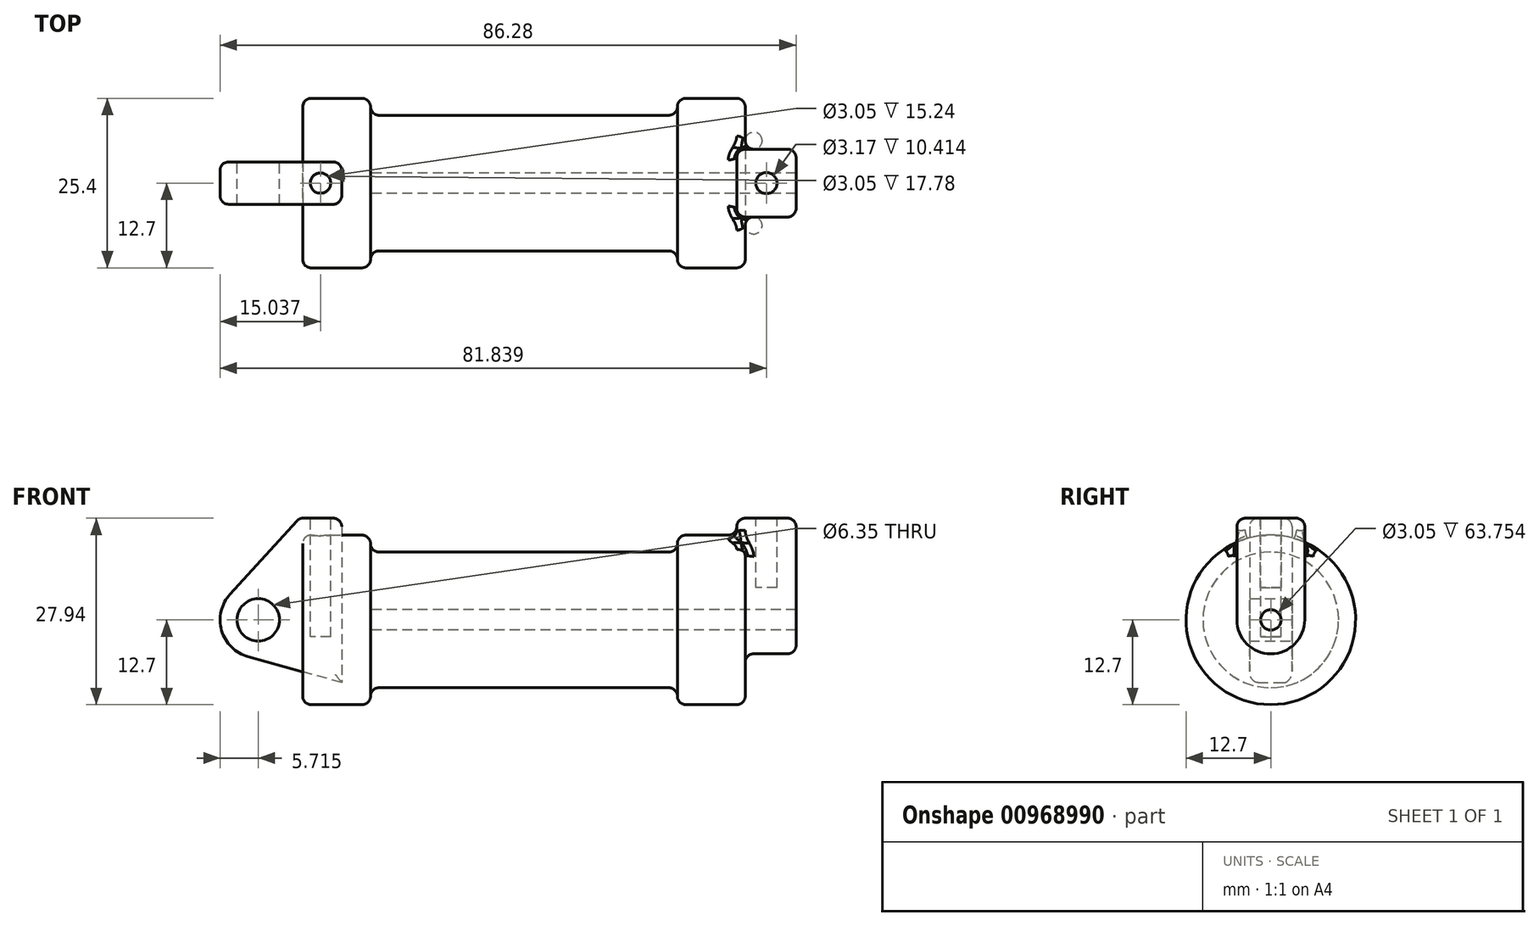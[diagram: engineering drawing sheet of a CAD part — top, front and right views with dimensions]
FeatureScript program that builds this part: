
annotation { "Feature Type Name" : "Feature", "Feature Type Description" : "" }
export const myFeature = defineFeature(function(context is Context, id is Id, definition is map)
    precondition{}
    {
        {
            var Q0;
            Q0=qCreatedBy(makeId("Front.planeOp"),FACE);
            var sketch = newSketch(context, id + "F0", { "sketchPlane" : qUnion([Q0])});
            skLineSegment(sketch, "E0", {"start": v(0, 0) * mm, "end": v(0, 12.7) * mm});
            skLineSegment(sketch, "E1", {"start": v(0, 12.7) * mm, "end": v(10.16, 12.7) * mm});
            skLineSegment(sketch, "E2", {"start": v(10.16, 12.7) * mm, "end": v(10.16, 10.16) * mm});
            skLineSegment(sketch, "E3", {"start": v(10.16, 10.16) * mm, "end": v(56.13, 10.16) * mm});
            skLineSegment(sketch, "E4", {"start": v(56.13, 10.16) * mm, "end": v(56.13, 12.7) * mm});
            skLineSegment(sketch, "E5", {"start": v(56.13, 12.7) * mm, "end": v(66.3, 12.7) * mm});
            skLineSegment(sketch, "E6", {"start": v(66.3, 12.7) * mm, "end": v(66.3, 0) * mm});
            skLineSegment(sketch, "E7", {"start": v(66.3, 0) * mm, "end": v(0, 0) * mm});
            skLineSegment(sketch, "E8", {"start": v(5.84, 15.24) * mm, "end": v(-0.5, 15.24) * mm});
            skLineSegment(sketch, "E9", {"start": v(-0.5, 15.24) * mm, "end": v(-10.88, 3.85) * mm});
            skLineSegment(sketch, "E10", {"start": v(0, 0) * mm, "end": v(-6.65, 0) * mm});
            skCircle(sketch, "E11", {"center": v(-6.65, 0) * mm, "radius": 5.72 * mm});
            skCircle(sketch, "E12", {"center": v(-6.65, 0) * mm, "radius": 3.18 * mm});
            skLineSegment(sketch, "E13", {"start": v(5.84, 15.24) * mm, "end": v(5.84, -9.4) * mm});
            skLineSegment(sketch, "E14", {"start": v(5.84, -9.4) * mm, "end": v(-8.18, -5.5) * mm});
            skSolve(sketch);
        }
        {
            var Q0;
            {var subQ0=sQuery(id+"F0.wireOp",EDGE,"E0");Q0=makeQuery(id+"F0.imprint","IMPRINT",FACE,{"disambiguationData":[TD([[makeQuery(id+"F0.imprint","IMPRINT",EDGE,{"derivedFrom":subQ0}),-1.0]])]});}
            var Q1;
            {var subQ1=sQuery(id+"F0.wireOp",EDGE,"E0");Q1=makeQuery(id+"F0.imprint","IMPRINT",FACE,{"disambiguationData":[TD([[makeQuery(id+"F0.imprint","IMPRINT",EDGE,{"derivedFrom":subQ1}),1.0]])]});}
            var Q2;
            {var subQ5=sQuery(id+"F0.wireOp",EDGE,"E12");Q2=makeQuery(id+"F0.imprint","IMPRINT",FACE,{"disambiguationData":[TD([[makeQuery(id+"F0.imprint","IMPRINT",EDGE,{"derivedFrom":subQ5}),-1.0]])]});}
            var Q3;
            {var subQ0=sQuery(id+"F0.wireOp",EDGE,"E14");Q3=makeQuery(id+"F0.imprint","IMPRINT",FACE,{"disambiguationData":[TD([[makeQuery(id+"F0.imprint","IMPRINT",EDGE,{"derivedFrom":subQ0}),-1.0]])]});}
            extrude(context, id + "F1", {"entities" : qUnion([Q0, Q1, Q2, Q3]), "endBound" : BoundingType.SYMMETRIC, "depth" : 6.35 * mm, "offsetDistance" : 25.4 * mm});
        }
        {
            var Q0;
            {var subQ0=sQuery(id+"F0.wireOp",EDGE,"E0");Q0=makeQuery(id+"F0.imprint","IMPRINT",FACE,{"disambiguationData":[TD([[makeQuery(id+"F0.imprint","IMPRINT",EDGE,{"derivedFrom":subQ0}),-1.0]])]});}
            var Q1;
            {var subQ0=sQuery(id+"F0.wireOp",EDGE,"E2");Q1=makeQuery(id+"F0.imprint","IMPRINT",FACE,{"disambiguationData":[TD([[makeQuery(id+"F0.imprint","IMPRINT",EDGE,{"derivedFrom":subQ0}),-1.0]])]});}
            var Q2;
            Q2=sQuery(id+"F0.wireOp",EDGE,"E7");
            revolve(context, id + "F2", {"surfaceOperationType" : NewSurfaceOperationType.NEW, "entities" : qUnion([Q0, Q1]), "axis" : qUnion([Q2]), "revolveType" : RevolveType.FULL});
        }
        {
            var Q0;
            Q0=makeQuery(id+"F2.opRevolve","SWEPT_FACE",FACE,{"disambiguationData":[OSD([sQuery(id+"F0.wireOp",EDGE,"E6")])]});
            var sketch = newSketch(context, id + "F3", { "sketchPlane" : qUnion([Q0])});
            skCircle(sketch, "E15", {"center": v(0, 0) * mm, "radius": 1.52 * mm});
            skCircle(sketch, "E16", {"center": v(0, 0) * mm, "radius": 5.08 * mm});
            skLineSegment(sketch, "E17", {"start": v(-5.08, 0) * mm, "end": v(-5.08, 15.24) * mm});
            skLineSegment(sketch, "E18", {"start": v(-5.08, 15.24) * mm, "end": v(5.08, 15.24) * mm});
            skLineSegment(sketch, "E19", {"start": v(5.08, 15.24) * mm, "end": v(5.08, 0) * mm});
            skSolve(sketch);
        }
        {
            var Q0;
            Q0 = qSketchRegion(id + "F3", true);
            extrude(context, id + "F4", {"entities" : qUnion([Q0]), "operationType" : NewBodyOperationType.ADD, "depth" : 7.62 * mm, "offsetDistance" : 25.4 * mm, "hasSecondDirection" : true, "secondDirectionOppositeDirection" : true, "secondDirectionDepth" : 1.27 * mm});
        }
        {
            var Q0;
            Q0=makeQuery(id+"F4.boolean.opBoolean","SPLIT",FACE,{"disambiguationData":[TD([makeQuery(id+"F4.opExtrude","SWEPT_FACE",FACE,{"disambiguationData":[OSD([sQuery(id+"F3.wireOp",EDGE,"E15")])]})])],"derivedFrom":makeQuery(id+"F2.opRevolve","SWEPT_FACE",FACE,{"disambiguationData":[OSD([sQuery(id+"F0.wireOp",EDGE,"E6")])]})});
            var Q1;
            Q1=makeQuery(id+"F2.opRevolve","SWEPT_FACE",FACE,{"disambiguationData":[OSD([sQuery(id+"F0.wireOp",EDGE,"E2")])]});
            extrude(context, id + "F5", {"entities" : qUnion([Q0]), "operationType" : NewBodyOperationType.REMOVE, "endBound" : BoundingType.UP_TO_SURFACE, "oppositeDirection" : true, "depth" : 25.4 * mm, "endBoundEntityFace" : qUnion([Q1]), "offsetDistance" : 25.4 * mm});
        }
        {
            var Q0;
            Q0=makeQuery(id+"F1.opExtrude","SWEPT_FACE",FACE,{"disambiguationData":[OSD([sQuery(id+"F0.wireOp",EDGE,"E8")])]});
            var sketch = newSketch(context, id + "F6", { "sketchPlane" : qUnion([Q0])});
            skCircle(sketch, "E20", {"center": v(2.67, 0) * mm, "radius": 1.52 * mm});
            skLineSegment(sketch, "E21", {"start": v(2.67, 0) * mm, "end": v(5.84, 0) * mm, "construction": true});
            skLineSegment(sketch, "E22", {"start": v(5.84, 0) * mm, "end": v(-0.5, 0) * mm, "construction": true});
            skLineSegment(sketch, "E23", {"start": v(-0.5, 0) * mm, "end": v(2.67, 0) * mm, "construction": true});
            skSolve(sketch);
        }
        {
            var Q0;
            Q0=makeQuery(id+"F6.imprint","IMPRINT",FACE,{"disambiguationData":[TD([[makeQuery(id+"F6.imprint","IMPRINT",EDGE,{"derivedFrom":sQuery(id+"F6.wireOp",EDGE,"E20")}),1.0]])]});
            extrude(context, id + "F7", {"entities" : qUnion([Q0]), "operationType" : NewBodyOperationType.REMOVE, "oppositeDirection" : true, "depth" : 17.78 * mm, "offsetDistance" : 25.4 * mm});
        }
        {
            var Q0;
            Q0=makeQuery(id+"F4.opExtrude","SWEPT_FACE",FACE,{"disambiguationData":[OSD([sQuery(id+"F3.wireOp",EDGE,"E18")])]});
            var sketch = newSketch(context, id + "F8", { "sketchPlane" : qUnion([Q0])});
            skCircle(sketch, "E24", {"center": v(69.47, 0) * mm, "radius": 1.59 * mm});
            skLineSegment(sketch, "E25", {"start": v(69.47, 0) * mm, "end": v(69.47, 5.08) * mm, "construction": true});
            skLineSegment(sketch, "E26", {"start": v(69.47, 0) * mm, "end": v(69.47, -5.08) * mm, "construction": true});
            skLineSegment(sketch, "E27", {"start": v(69.47, 0) * mm, "end": v(65.02, 0) * mm, "construction": true});
            skLineSegment(sketch, "E28", {"start": v(69.47, 0) * mm, "end": v(73.91, 0) * mm, "construction": true});
            skSolve(sketch);
        }
        {
            var Q0;
            Q0=makeQuery(id+"F8.imprint","IMPRINT",FACE,{"disambiguationData":[TD([[makeQuery(id+"F8.imprint","IMPRINT",EDGE,{"derivedFrom":sQuery(id+"F8.wireOp",EDGE,"E24")}),1.0]])]});
            extrude(context, id + "F9", {"entities" : qUnion([Q0]), "operationType" : NewBodyOperationType.REMOVE, "oppositeDirection" : true, "depth" : 10.4 * mm, "offsetDistance" : 25.4 * mm});
        }
        {
            var Q0;
            Q0=makeQuery(id+"F2.opRevolve","SWEPT_EDGE",EDGE,{"disambiguationData":[OSD([sQuery(id+"F0.wireOp",EDGE,"E0"),sQuery(id+"F0.wireOp",EDGE,"E1")])]});
            var Q1;
            Q1=makeQuery(id+"F2.opRevolve","SWEPT_EDGE",EDGE,{"disambiguationData":[OSD([sQuery(id+"F0.wireOp",EDGE,"E1"),sQuery(id+"F0.wireOp",EDGE,"E2")])]});
            var Q2;
            Q2=makeQuery(id+"F1.opExtrude","CAP_EDGE",EDGE,{"disambiguationData":[OSD([sQuery(id+"F0.wireOp",EDGE,"E8")])],"isStart":false});
            var Q3;
            Q3=makeQuery(id+"F1.opExtrude","CAP_EDGE",EDGE,{"disambiguationData":[OSD([sQuery(id+"F0.wireOp",EDGE,"E13")])],"isStart":false});
            var Q4;
            Q4=makeQuery(id+"F1.opExtrude","CAP_EDGE",EDGE,{"disambiguationData":[OSD([sQuery(id+"F0.wireOp",EDGE,"E9")])],"isStart":false});
            var Q5;
            Q5=makeQuery(id+"F1.opExtrude","SWEPT_EDGE",EDGE,{"disambiguationData":[OSD([sQuery(id+"F0.wireOp",EDGE,"E8"),sQuery(id+"F0.wireOp",EDGE,"E9")])]});
            var Q6;
            Q6=makeQuery(id+"F1.opExtrude","CAP_EDGE",EDGE,{"disambiguationData":[OSD([sQuery(id+"F0.wireOp",EDGE,"E8")])],"isStart":true});
            var Q7;
            Q7=makeQuery(id+"F1.opExtrude","CAP_EDGE",EDGE,{"disambiguationData":[OSD([sQuery(id+"F0.wireOp",EDGE,"E13")])],"isStart":true});
            var Q8;
            Q8=makeQuery(id+"F1.opExtrude","SWEPT_EDGE",EDGE,{"disambiguationData":[OSD([sQuery(id+"F0.wireOp",EDGE,"E8"),sQuery(id+"F0.wireOp",EDGE,"E13")])]});
            var Q9;
            Q9=makeQuery(id+"F1.opExtrude","CAP_EDGE",EDGE,{"disambiguationData":[OSD([sQuery(id+"F0.wireOp",EDGE,"E11")])],"isStart":false});
            var Q10;
            Q10=makeQuery(id+"F1.opExtrude","CAP_EDGE",EDGE,{"disambiguationData":[OSD([sQuery(id+"F0.wireOp",EDGE,"E11")])],"isStart":true});
            var Q11;
            Q11=makeQuery(id+"F1.opExtrude","CAP_EDGE",EDGE,{"disambiguationData":[OSD([sQuery(id+"F0.wireOp",EDGE,"E14")])],"isStart":false});
            var Q12;
            Q12=makeQuery(id+"F2.opRevolve","SWEPT_EDGE",EDGE,{"disambiguationData":[OSD([sQuery(id+"F0.wireOp",EDGE,"E2"),sQuery(id+"F0.wireOp",EDGE,"E3")])]});
            var Q13;
            Q13=makeQuery(id+"F2.opRevolve","SWEPT_EDGE",EDGE,{"disambiguationData":[OSD([sQuery(id+"F0.wireOp",EDGE,"E3"),sQuery(id+"F0.wireOp",EDGE,"E4")])]});
            var Q14;
            Q14=makeQuery(id+"F2.opRevolve","SWEPT_EDGE",EDGE,{"disambiguationData":[OSD([sQuery(id+"F0.wireOp",EDGE,"E4"),sQuery(id+"F0.wireOp",EDGE,"E5")])]});
            var Q15;
            Q15=makeQuery(id+"F2.opRevolve","SWEPT_EDGE",EDGE,{"disambiguationData":[OSD([sQuery(id+"F0.wireOp",EDGE,"E5"),sQuery(id+"F0.wireOp",EDGE,"E6")])]});
            var Q16;
            Q16=makeQuery(id+"F4.opExtrude","CAP_EDGE",EDGE,{"disambiguationData":[OSD([sQuery(id+"F3.wireOp",EDGE,"E17")])],"isStart":true});
            var Q17;
            Q17=makeQuery(id+"F4.opExtrude","SWEPT_EDGE",EDGE,{"disambiguationData":[OSD([sQuery(id+"F3.wireOp",EDGE,"E17"),sQuery(id+"F3.wireOp",EDGE,"E18")])]});
            var Q18;
            Q18=makeQuery(id+"F4.opExtrude","CAP_EDGE",EDGE,{"disambiguationData":[OSD([sQuery(id+"F3.wireOp",EDGE,"E17")])],"isStart":false});
            var Q19;
            Q19=makeQuery(id+"F4.boolean.opBoolean","SPLIT",FACE,{"disambiguationData":[TD([makeQuery(id+"F2.opRevolve","SWEPT_FACE",FACE,{"disambiguationData":[OSD([sQuery(id+"F0.wireOp",EDGE,"E5")])]})])],"derivedFrom":makeQuery(id+"F2.opRevolve","SWEPT_FACE",FACE,{"disambiguationData":[OSD([sQuery(id+"F0.wireOp",EDGE,"E6")])]})});
            var Q20;
            Q20=makeQuery(id+"F4.opExtrude","CAP_EDGE",EDGE,{"disambiguationData":[OSD([sQuery(id+"F3.wireOp",EDGE,"E16")])],"isStart":false});
            var Q21;
            Q21=makeQuery(id+"F4.opExtrude","CAP_EDGE",EDGE,{"disambiguationData":[OSD([sQuery(id+"F3.wireOp",EDGE,"E19")])],"isStart":false});
            var Q22;
            Q22=makeQuery(id+"F4.opExtrude","SWEPT_EDGE",EDGE,{"disambiguationData":[OSD([sQuery(id+"F3.wireOp",EDGE,"E18"),sQuery(id+"F3.wireOp",EDGE,"E19")])]});
            var Q23;
            Q23=makeQuery(id+"F4.opExtrude","CAP_EDGE",EDGE,{"disambiguationData":[OSD([sQuery(id+"F3.wireOp",EDGE,"E18")])],"isStart":false});
            var Q24;
            Q24=makeQuery(id+"F4.opExtrude","CAP_EDGE",EDGE,{"disambiguationData":[OSD([sQuery(id+"F3.wireOp",EDGE,"E18")])],"isStart":true});
            var Q25;
            Q25=makeQuery(id+"F4.opExtrude","CAP_EDGE",EDGE,{"disambiguationData":[OSD([sQuery(id+"F3.wireOp",EDGE,"E19")])],"isStart":true});
            var Q26;
            Q26=makeQuery(id+"F4.boolean.opBoolean","INTERSECT",EDGE,{"derivedFrom":[makeQuery(id+"F2.opRevolve","SWEPT_FACE",FACE,{"disambiguationData":[OSD([sQuery(id+"F0.wireOp",EDGE,"E5")])]}),makeQuery(id+"F4.opExtrude","CAP_FACE",FACE,{"disambiguationData":[OSD([sQuery(id+"F3.wireOp",EDGE,"E15"),sQuery(id+"F3.wireOp",EDGE,"E16"),sQuery(id+"F3.wireOp",EDGE,"E17"),sQuery(id+"F3.wireOp",EDGE,"E18"),sQuery(id+"F3.wireOp",EDGE,"E19")])],"isStart":true})]});
            var Q27;
            Q27=makeQuery(id+"F4.boolean.opBoolean","INTERSECT",EDGE,{"derivedFrom":[makeQuery(id+"F2.opRevolve","SWEPT_FACE",FACE,{"disambiguationData":[OSD([sQuery(id+"F0.wireOp",EDGE,"E5")])]}),makeQuery(id+"F4.opExtrude","SWEPT_FACE",FACE,{"disambiguationData":[OSD([sQuery(id+"F3.wireOp",EDGE,"E19")])]})]});
            var Q28;
            Q28=makeQuery(id+"F4.boolean.opBoolean","INTERSECT",EDGE,{"derivedFrom":[makeQuery(id+"F2.opRevolve","SWEPT_FACE",FACE,{"disambiguationData":[OSD([sQuery(id+"F0.wireOp",EDGE,"E5")])]}),makeQuery(id+"F4.opExtrude","SWEPT_FACE",FACE,{"disambiguationData":[OSD([sQuery(id+"F3.wireOp",EDGE,"E17")])]})]});
            var Q29;
            Q29=makeQuery(id+"F2.opRevolve","SWEPT_FACE",FACE,{"disambiguationData":[OSD([sQuery(id+"F0.wireOp",EDGE,"E0")])]});
            fillet(context, id + "F10", {"entities" : qUnion([Q0, Q1, Q2, Q3, Q4, Q5, Q6, Q7, Q8, Q9, Q10, Q11, Q12, Q13, Q14, Q15, Q16, Q17, Q18, Q19, Q20, Q21, Q22, Q23, Q24, Q25, Q26, Q27, Q28, Q29]), "radius" : 1.27 * mm, "tangentPropagation" : true, "allowEdgeOverflow" : false});
        }
    });
